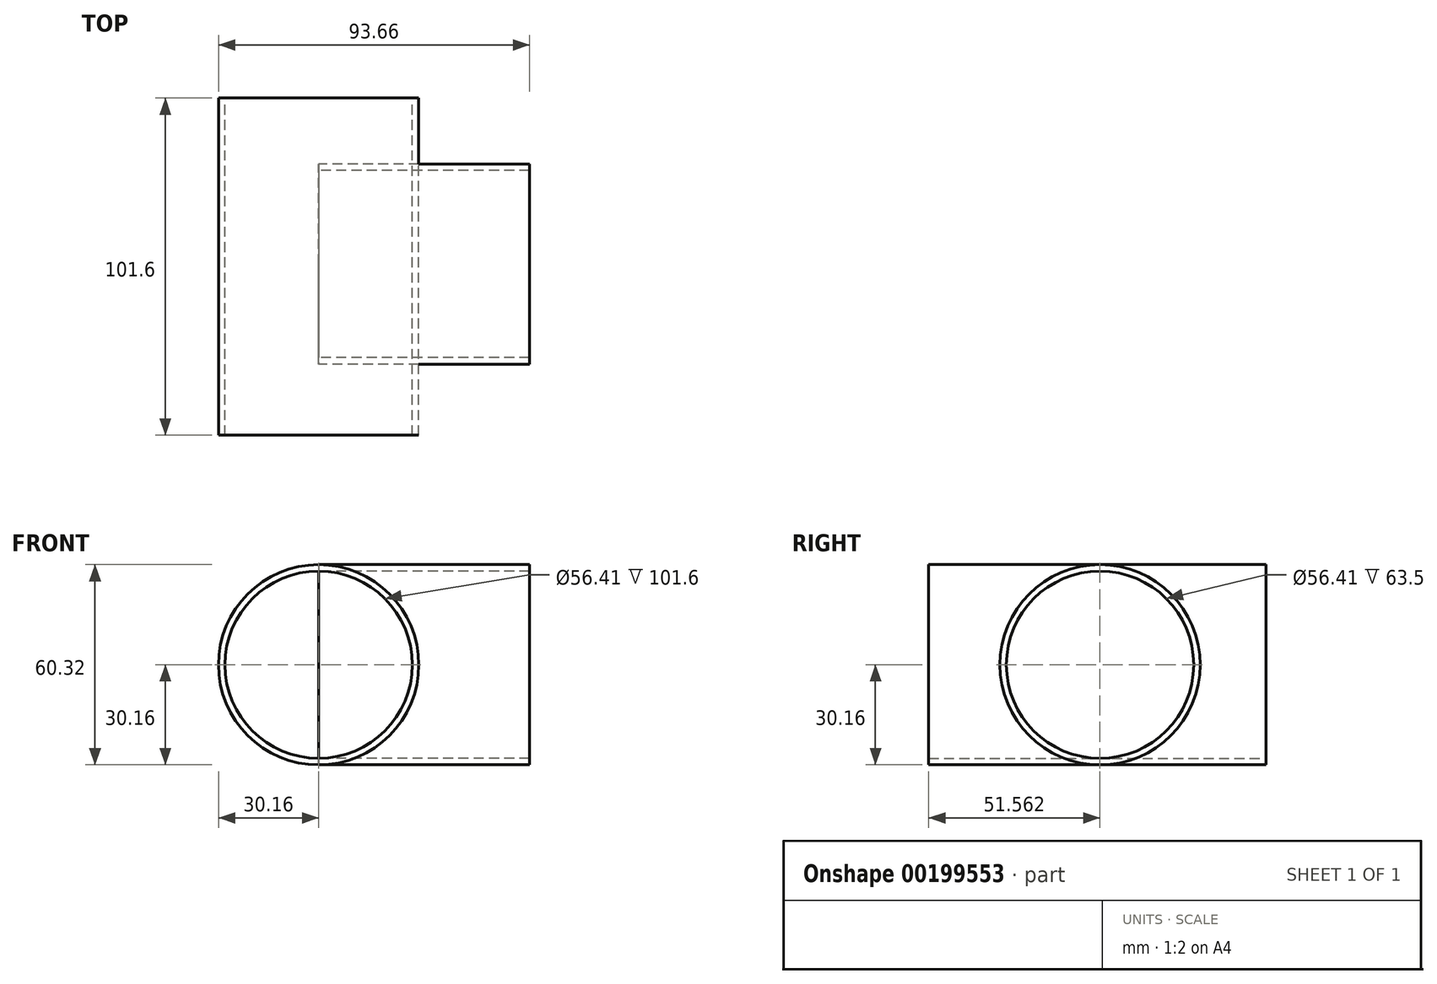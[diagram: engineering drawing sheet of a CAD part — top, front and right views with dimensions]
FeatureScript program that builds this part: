
annotation { "Feature Type Name" : "Feature", "Feature Type Description" : "" }
export const myFeature = defineFeature(function(context is Context, id is Id, definition is map)
    precondition{}
    {
        {
            var Q0;
            Q0=qCreatedBy(makeId("Front.planeOp"),FACE);
            var sketch = newSketch(context, id + "F0", { "sketchPlane" : qUnion([Q0])});
            skCircle(sketch, "E0", {"center": v(0, 0) * mm, "radius": 28.2 * mm});
            skCircle(sketch, "E1", {"center": v(0, 0) * mm, "radius": 30.16 * mm});
            skSolve(sketch);
        }
        {
            var Q0;
            Q0=makeQuery(id+"F0.imprint","IMPRINT",FACE,{"disambiguationData":[TD([[makeQuery(id+"F0.imprint","IMPRINT",EDGE,{"derivedFrom":sQuery(id+"F0.wireOp",EDGE,"E0")}),-1.0]])]});
            extrude(context, id + "F1", {"entities" : qUnion([Q0]), "depth" : 101.6 * mm});
        }
        {
            var Q0;
            Q0=qCreatedBy(makeId("Right.planeOp"),FACE);
            var sketch = newSketch(context, id + "F2", { "sketchPlane" : qUnion([Q0])});
            skCircle(sketch, "E2", {"center": v(0, 0) * mm, "radius": 28.2 * mm});
            skCircle(sketch, "E3", {"center": v(0, 0) * mm, "radius": 30.16 * mm});
            skSolve(sketch);
        }
        {
            var Q0;
            Q0 = qSketchRegion(id + "F2", true);
            extrude(context, id + "F3", {"entities" : qUnion([Q0]), "depth" : 63.5 * mm});
        }
        {
            var Q0;
            Q0=makeQuery(id+"F3.opExtrude","SWEPT_BODY",BODY,{"disambiguationData":[OSD([sQuery(id+"F2.wireOp",EDGE,"E2"),sQuery(id+"F2.wireOp",EDGE,"E3")])]});
            transform(context, id + "F4", {"entities" : qUnion([Q0]), "transformType" : TransformType.TRANSLATION_3D, "dx" : 0 * mm, "dy" : -50.04 * mm, "dz" : 0 * mm, "makeCopy" : false});
        }
    });
